# Revit family: IS_TonicII_R4320_BIM_FR
name_source: partatom
category: Plumbing Fixtures
revit_build: Autodesk Revit 2017 (Build: 20160225_1515(x64)
units: mm (PartAtom-declared; Revit-internal decimal feet)

## family parameters
Always vertical = No
Cut with Voids When Loaded = No
OmniClass Number = 23.40.20.00
OmniClass Title = General Furniture and Specialties
Part Type = Normal
Room Calculation Point = No
Round Connector Dimension = Use Diameter
Shared = No
Work Plane-Based = No

## types (5) — shared parameters
Accessoires = www.idealstandard.be
Auteur = Ideal Standard
BOSUseNativeGeometries = 1
Caractéristiques = TONIC II WORKTOP 500 GLS LGY BSN ST SHLF
CodeBarre = 3391500572676
ConseilsDInstallation = www.idealstandard.be
Couleur = L Grey
DateDeCréation = 2018_08_15
Description = TONIC II Plan étagère 50 cm
Espace = Interne
Finition = L Grey
Forme = Complexe
Hauteur = 12 mm  [stored 0.0393701 ft]
IfcExportAs = FURNITURE
IfcExportType = IfcSanitaryTerminalType
InformationsProduit = www.idealstandard.be
Largeur = 502 mm  [stored 1.64698 ft]
LienUtile = www.idealstandard.be
Longueur = 364 mm  [stored 1.19423 ft]
Manufacturer = www.idealstandard.be
Marque = Ideal Standard
Matériel = Wood
Raccordement = Plomberie
Révision = 1
URL = www.idealstandard.be
Uniclass2015Code = Pr_40_20_76_94
Uniclass2015Title = Vanity units
Uniclass2015Version = Products v1.1
UnitéDeMesure = Millimètres
UnitéDeTemps = An
UnitéMonétaire = €
UrlDuFabricant = www.idealstandard.be
Version = 1
zero-valued in all types: Cost, CoûtDeRemplacement, Profondeur

## per-type parameters (varying)
| type | Bim-NomDuProjet | Dimensions | Model |
| R4320FA - TONIC II PLAN ETAGERE 50CM GRIS BRILLANT | ISI_IdealStandard_VanityUnits_TONIC_R4320FC | 12 X 502 X 364 mm | R4320FC |
| R4320FC - TONIC II PLAN ETAGERE 50CM SABLON BRILL | ISI_IdealStandard_VanityUnits_TONIC_R4320FE | 12 X 502 X 364 mm | R4320FE |
| R4320FE - TONIC II PLAN ETAGERE 50CM CHENE GRISE | ISI_IdealStandard_VanityUnits_TONIC_R4320FF | 12 X 502 X 364 mm | R4320FF |
| R4320FF - TONIC II PLAN ETAGERE 50CM CHENE CERUSE | ISI_IdealStandard_VanityUnits_TONIC_R4320WG | 12 x 502 x 364 mm | R4320WG |
| R4320WG - TONIC II PLAN ETAGERE 50CM BLANC BRILL | ISI_IdealStandard_VanityUnits_TONIC_R4320WG | 12 X 502 X 364 mm | R4320WG |

note: [stored X ft] marks values corroborated as IEEE doubles in the binary element streams (Revit-internal decimal feet)

## geometry (parser evidence)
native form markers: Sweep x2
no freeform markers — native parametric forms only
